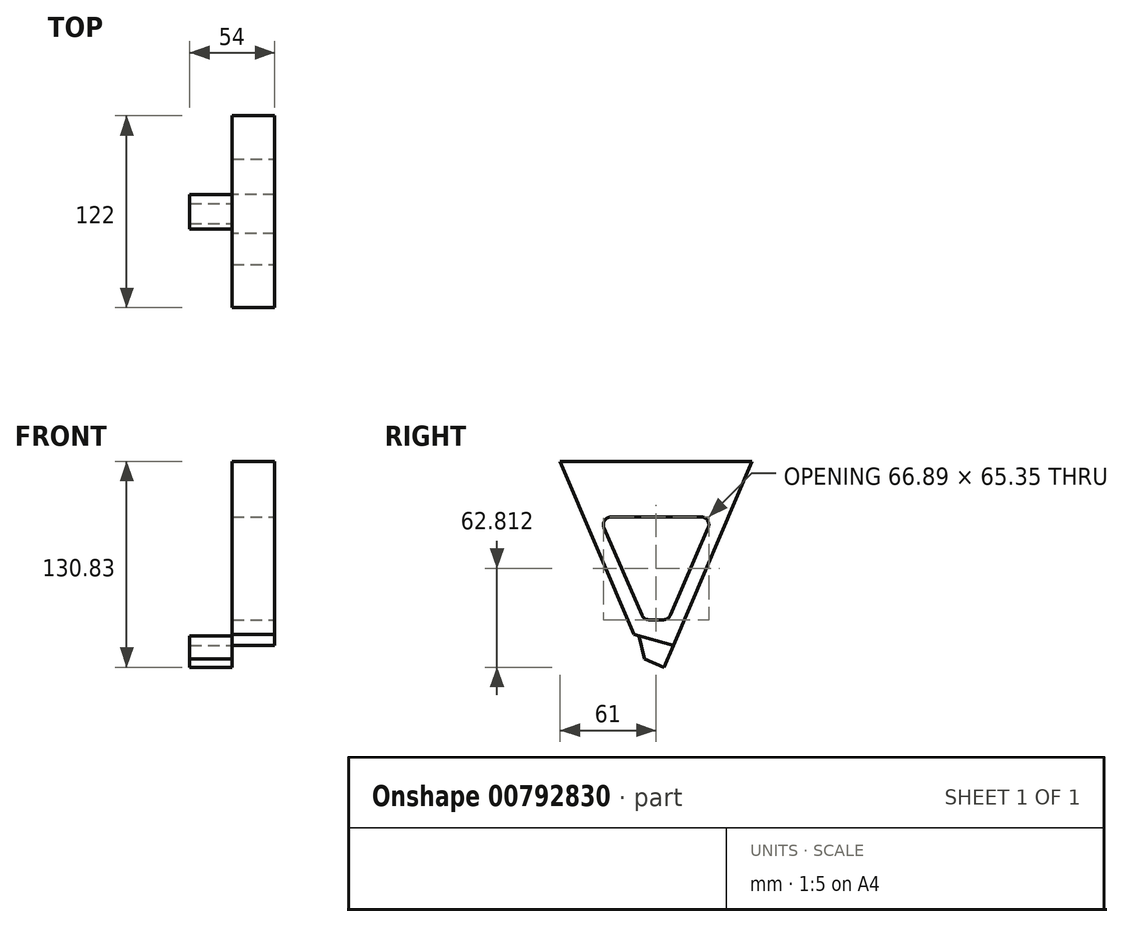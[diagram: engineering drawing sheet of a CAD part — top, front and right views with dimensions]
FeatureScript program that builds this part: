
annotation { "Feature Type Name" : "Feature", "Feature Type Description" : "" }
export const myFeature = defineFeature(function(context is Context, id is Id, definition is map)
    precondition{}
    {
        {
            var Q0;
            Q0=qCreatedBy(makeId("Right.planeOp"),FACE);
            var sketch = newSketch(context, id + "F0", { "sketchPlane" : qUnion([Q0])});
            skLineSegment(sketch, "E0", {"start": v(0, 72.87) * mm, "end": v(0, -66.18) * mm, "construction": true});
            skLineSegment(sketch, "E1", {"start": v(69.02, 0) * mm, "end": v(-69.36, 0) * mm, "construction": true});
            skLineSegment(sketch, "E2", {"start": v(0, 44.26) * mm, "end": v(-61, 44.26) * mm});
            skLineSegment(sketch, "E3", {"start": v(0, 44.26) * mm, "end": v(0, -79.74) * mm});
            skLineSegment(sketch, "E4", {"start": v(0, -65.74) * mm, "end": v(-14, -65.74) * mm});
            skLineSegment(sketch, "E5", {"start": v(-61, 44.26) * mm, "end": v(-14, -65.74) * mm});
            skLineSegment(sketch, "E6.MirrorCS", {"start": v(0, 44.26) * mm, "end": v(61, 44.26) * mm});
            skLineSegment(sketch, "E7.MirrorCS", {"start": v(61, 44.26) * mm, "end": v(14, -65.74) * mm});
            skLineSegment(sketch, "E8.MirrorCS", {"start": v(0, -65.74) * mm, "end": v(14, -65.74) * mm});
            skLineSegment(sketch, "E9", {"start": v(14, -65.74) * mm, "end": v(11.06, -72.62) * mm});
            skLineSegment(sketch, "E10", {"start": v(11.06, -72.62) * mm, "end": v(-14, -65.74) * mm});
            skSolve(sketch);
        }
        {
            var Q0;
            Q0 = qSketchRegion(id + "F0", true);
            extrude(context, id + "F1", {"entities" : qUnion([Q0]), "depth" : 27 * mm, "offsetDistance" : 25 * mm});
        }
        {
            var Q0;
            Q0=makeQuery(id+"F1.opExtrude","CAP_FACE",FACE,{"disambiguationData":[OSD([sQuery(id+"F0.wireOp",EDGE,"E2"),sQuery(id+"F0.wireOp",EDGE,"E4"),sQuery(id+"F0.wireOp",EDGE,"E5"),sQuery(id+"F0.wireOp",EDGE,"E6.MirrorCS"),sQuery(id+"F0.wireOp",EDGE,"E7.MirrorCS"),sQuery(id+"F0.wireOp",EDGE,"E8.MirrorCS")])],"isStart":false});
            var sketch = newSketch(context, id + "F2", { "sketchPlane" : qUnion([Q0])});
            skLineSegment(sketch, "E11", {"start": v(68.47, 44.26) * mm, "end": v(-24.32, 44.26) * mm, "construction": true});
            skLineSegment(sketch, "E12", {"start": v(-36.07, 8.92) * mm, "end": v(36.07, 8.92) * mm});
            skLineSegment(sketch, "E13", {"start": v(7.82, -56.43) * mm, "end": v(-7.82, -56.43) * mm});
            skLineSegment(sketch, "E14", {"start": v(-36.07, 8.92) * mm, "end": v(-7.82, -56.43) * mm});
            skLineSegment(sketch, "E15", {"start": v(7.82, -56.43) * mm, "end": v(36.07, 8.92) * mm});
            skSolve(sketch);
        }
        {
            var Q0;
            Q0 = qSketchRegion(id + "F2", true);
            extrude(context, id + "F3", {"entities" : qUnion([Q0]), "operationType" : NewBodyOperationType.REMOVE, "oppositeDirection" : true, "depth" : 30 * mm, "offsetDistance" : 25 * mm});
        }
        {
            var Q0;
            Q0=makeQuery(id+"F3.boolean.opBoolean","COPY",EDGE,{"derivedFrom":makeQuery(id+"F3.opExtrude","SWEPT_EDGE",EDGE,{"disambiguationData":[OSD([sQuery(id+"F2.wireOp",EDGE,"E12"),sQuery(id+"F2.wireOp",EDGE,"E14")])]})});
            var Q1;
            Q1=makeQuery(id+"F3.boolean.opBoolean","COPY",EDGE,{"derivedFrom":makeQuery(id+"F3.opExtrude","SWEPT_EDGE",EDGE,{"disambiguationData":[OSD([sQuery(id+"F2.wireOp",EDGE,"E12"),sQuery(id+"F2.wireOp",EDGE,"E15")])]})});
            var Q2;
            Q2=makeQuery(id+"F3.boolean.opBoolean","COPY",EDGE,{"derivedFrom":makeQuery(id+"F3.opExtrude","SWEPT_EDGE",EDGE,{"disambiguationData":[OSD([sQuery(id+"F2.wireOp",EDGE,"E13"),sQuery(id+"F2.wireOp",EDGE,"E14")])]})});
            var Q3;
            Q3=makeQuery(id+"F3.boolean.opBoolean","COPY",EDGE,{"derivedFrom":makeQuery(id+"F3.opExtrude","SWEPT_EDGE",EDGE,{"disambiguationData":[OSD([sQuery(id+"F2.wireOp",EDGE,"E13"),sQuery(id+"F2.wireOp",EDGE,"E15")])]})});
            fillet(context, id + "F4", {"entities" : qUnion([Q0, Q1, Q2, Q3]), "tangentPropagation" : true, "radius" : 5 * mm, "defaultsChanged" : false, "vertexSettings" : [], "allowEdgeOverflow" : false});
        }
        {
            var Q0;
            Q0=makeQuery(id+"F1.opExtrude","CAP_FACE",FACE,{"disambiguationData":[OSD([sQuery(id+"F0.wireOp",EDGE,"E2"),sQuery(id+"F0.wireOp",EDGE,"E5"),sQuery(id+"F0.wireOp",EDGE,"E6.MirrorCS"),sQuery(id+"F0.wireOp",EDGE,"E7.MirrorCS"),sQuery(id+"F0.wireOp",EDGE,"E9"),sQuery(id+"F0.wireOp",EDGE,"E10")])],"isStart":true});
            var sketch = newSketch(context, id + "F5", { "sketchPlane" : qUnion([Q0])});
            skLineSegment(sketch, "E16", {"start": v(-11.06, -72.62) * mm, "end": v(-5.1, -86.57) * mm});
            skLineSegment(sketch, "E17", {"start": v(-5.1, -86.57) * mm, "end": v(7.5, -81.18) * mm});
            skLineSegment(sketch, "E18", {"start": v(7.5, -81.18) * mm, "end": v(10.98, -66.57) * mm});
            skLineSegment(sketch, "E19", {"start": v(-11.06, -72.62) * mm, "end": v(10.98, -66.57) * mm});
            skSolve(sketch);
        }
        {
            var Q0;
            Q0 = qSketchRegion(id + "F5", true);
            extrude(context, id + "F6", {"entities" : qUnion([Q0]), "depth" : 27 * mm, "offsetDistance" : 25 * mm});
        }
    });
